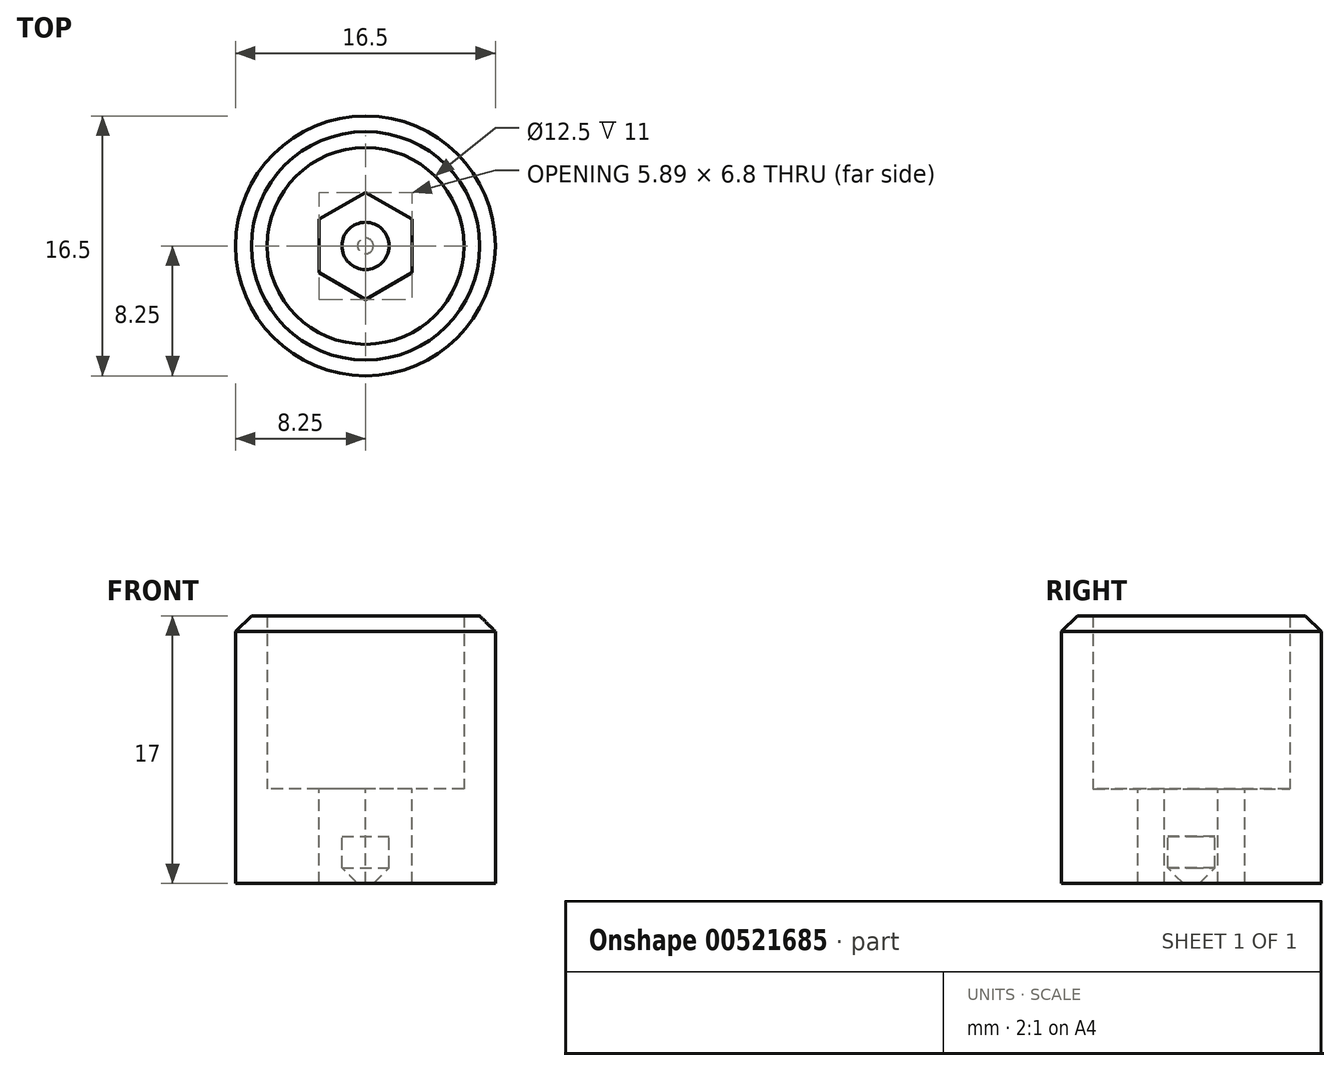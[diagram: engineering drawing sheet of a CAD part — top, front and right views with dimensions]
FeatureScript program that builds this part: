
annotation { "Feature Type Name" : "Feature", "Feature Type Description" : "" }
export const myFeature = defineFeature(function(context is Context, id is Id, definition is map)
    precondition{}
    {
        {
            var Q0;
            Q0=qCreatedBy(makeId("Top.planeOp"),FACE);
            var sketch = newSketch(context, id + "F0", { "sketchPlane" : qUnion([Q0])});
            skCircle(sketch, "E0", {"center": v(0, 0) * mm, "radius": 6.25 * mm});
            skCircle(sketch, "E1.0", {"center": v(0, 0) * mm, "radius": 8.25 * mm});
            skCircle(sketch, "E2.cCircle", {"center": v(0, 0) * mm, "radius": 3.4 * mm, "construction": true});
            skLineSegment(sketch, "E2.0", {"start": v(0, -3.4) * mm, "end": v(-2.94, -1.7) * mm});
            skLineSegment(sketch, "E2.1", {"start": v(-2.94, -1.7) * mm, "end": v(-2.94, 1.7) * mm});
            skLineSegment(sketch, "E2.2", {"start": v(-2.94, 1.7) * mm, "end": v(0, 3.4) * mm});
            skLineSegment(sketch, "E2.3", {"start": v(0, 3.4) * mm, "end": v(2.94, 1.7) * mm});
            skLineSegment(sketch, "E2.4", {"start": v(2.94, 1.7) * mm, "end": v(2.94, -1.7) * mm});
            skLineSegment(sketch, "E2.5", {"start": v(2.94, -1.7) * mm, "end": v(0, -3.4) * mm});
            skCircle(sketch, "E3", {"center": v(0, 0) * mm, "radius": 1.5 * mm});
            skSolve(sketch);
        }
        {
            var Q0;
            Q0 = qSketchRegion(id + "F0", true);
            extrude(context, id + "F1", {"entities" : qUnion([Q0]), "depth" : 11 * mm, "offsetDistance" : 25 * mm});
        }
        {
            var Q0;
            Q0=makeQuery(id+"F0.imprint","IMPRINT",FACE,{"disambiguationData":[TD([[makeQuery(id+"F0.imprint","IMPRINT",EDGE,{"derivedFrom":sQuery(id+"F0.wireOp",EDGE,"E0")}),1.0]])]});
            var Q1;
            Q1=makeQuery(id+"F0.imprint","IMPRINT",FACE,{"disambiguationData":[TD([[makeQuery(id+"F0.imprint","IMPRINT",EDGE,{"derivedFrom":sQuery(id+"F0.wireOp",EDGE,"E0")}),-1.0]])]});
            extrude(context, id + "F2", {"entities" : qUnion([Q0, Q1]), "operationType" : NewBodyOperationType.ADD, "oppositeDirection" : true, "depth" : 3 * mm, "offsetDistance" : 25 * mm});
        }
        {
            var Q0;
            Q0=makeQuery(id+"F2.opExtrude","CAP_FACE",FACE,{"disambiguationData":[OSD([sQuery(id+"F0.wireOp",EDGE,"E1.0"),sQuery(id+"F0.wireOp",EDGE,"E2.0"),sQuery(id+"F0.wireOp",EDGE,"E2.1"),sQuery(id+"F0.wireOp",EDGE,"E2.2"),sQuery(id+"F0.wireOp",EDGE,"E2.3"),sQuery(id+"F0.wireOp",EDGE,"E2.4"),sQuery(id+"F0.wireOp",EDGE,"E2.5")])],"isStart":false});
            var sketch = newSketch(context, id + "F3", { "sketchPlane" : qUnion([Q0])});
            skCircle(sketch, "E4.0", {"center": v(0, 0) * mm, "radius": 1.5 * mm});
            skCircle(sketch, "E5.0", {"center": v(0, 0) * mm, "radius": 8.25 * mm});
            skSolve(sketch);
        }
        {
            var Q0;
            Q0=makeQuery(id+"F3.imprint","IMPRINT",FACE,{"disambiguationData":[TD([[makeQuery(id+"F3.imprint","IMPRINT",EDGE,{"derivedFrom":sQuery(id+"F3.wireOp",EDGE,"E5.0")}),-1.0]])]});
            var Q1;
            Q1=makeQuery(id+"F3.imprint","IMPRINT",FACE,{"disambiguationData":[TD([[makeQuery(id+"F3.imprint","IMPRINT",EDGE,{"derivedFrom":sQuery(id+"F3.wireOp",EDGE,"E4.0")}),1.0]])]});
            extrude(context, id + "F4", {"entities" : qUnion([Q0, Q1]), "operationType" : NewBodyOperationType.ADD, "depth" : 3 * mm, "offsetDistance" : 25 * mm});
        }
        {
            var Q0;
            {var subQ0=sQuery(id+"F60BZsk967ldNyW_1.wireOp",EDGE,"BexA0TVl-CrZN-lgpx-OB4C-7qtbFCR5rZC3");var subQ1=sQuery(id+"F60BZsk967ldNyW_1.wireOp",EDGE,"fOaTZAAm-BOGP-XpJu-J1Rj-cpzaZgBpud2N");var subQ2=sQuery(id+"F3.wireOp",EDGE,"E5.0");var subQ3=sQuery(id+"F60BZsk967ldNyW_1.wireOp",EDGE,"IQxrd69i-Ddg1-UNJ9-Im6p-Feff2rNmEmPS");var subQ4=sQuery(id+"F60BZsk967ldNyW_1.wireOp",EDGE,"urlR4o0v-2UyR-yoqs-tff4-UfpLfiPC5AHg");Q0=makeQuery(id+"FydpxLhHa45ckt6_1.boolean.opBoolean","MERGE",FACE,{"derivedFrom":[makeQuery(id+"F4.opExtrude","CAP_FACE",FACE,{"disambiguationData":[OSD([sQuery(id+"F3.wireOp",EDGE,"E4.0"),subQ2])],"isStart":false}),makeQuery(id+"FydpxLhHa45ckt6_1.opExtrude","CAP_FACE",FACE,{"disambiguationData":[OSD([subQ2,subQ4,subQ3,sQuery(id+"F60BZsk967ldNyW_1.wireOp",EDGE,"1R1nssS0-jsyz-3M8a-dof1-n1xkOVE5Fvd1")])],"isStart":true}),makeQuery(id+"FydpxLhHa45ckt6_1.opExtrude","CAP_FACE",FACE,{"disambiguationData":[OSD([subQ2,subQ4,subQ3,sQuery(id+"F60BZsk967ldNyW_1.wireOp",EDGE,"xyycS0MH-joeu-DzFu-PEpD-GEJ9mzbRAiye")])],"isStart":true}),makeQuery(id+"FydpxLhHa45ckt6_1.opExtrude","CAP_FACE",FACE,{"disambiguationData":[OSD([subQ2,subQ1,subQ0,sQuery(id+"F60BZsk967ldNyW_1.wireOp",EDGE,"DkyQlpwt-tWpm-aolS-qxVb-v4OLD6zFZo6k")])],"isStart":true}),makeQuery(id+"FydpxLhHa45ckt6_1.opExtrude","CAP_FACE",FACE,{"disambiguationData":[OSD([subQ2,subQ1,subQ0,sQuery(id+"F60BZsk967ldNyW_1.wireOp",EDGE,"TKd5Jph9-hZX0-TMZX-mLID-D2HJWPI7puQZ")])],"isStart":true})]});}
            var Q1;
            Q1=makeQuery(id+"F1.opExtrude","CAP_EDGE",EDGE,{"disambiguationData":[OSD([sQuery(id+"F0.wireOp",EDGE,"E1.0")])],"isStart":false});
            chamfer(context, id + "F5", {"entities" : qUnion([Q0, Q1]), "width" : 1 * mm, "tangentPropagation" : true});
        }
    });
